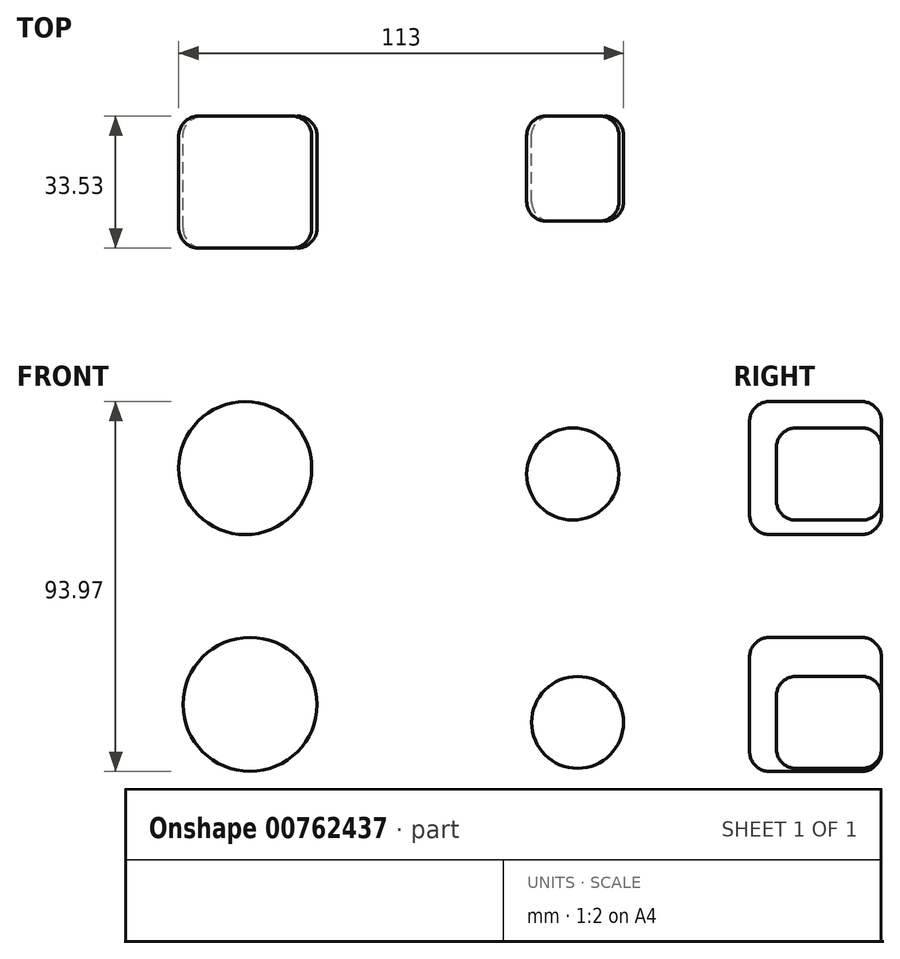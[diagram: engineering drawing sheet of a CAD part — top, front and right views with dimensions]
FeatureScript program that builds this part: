
annotation { "Feature Type Name" : "Feature", "Feature Type Description" : "" }
export const myFeature = defineFeature(function(context is Context, id is Id, definition is map)
    precondition{}
    {
        {
            var Q0;
            Q0=qCreatedBy(makeId("Front.planeOp"),FACE);
            var sketch = newSketch(context, id + "F0", { "sketchPlane" : qUnion([Q0])});
            skCircle(sketch, "E0", {"center": v(-51.36, 33.22) * mm, "radius": 16.9 * mm});
            skCircle(sketch, "E1", {"center": v(-50.14, -26.82) * mm, "radius": 17.03 * mm});
            skCircle(sketch, "E2", {"center": v(31.85, 31.7) * mm, "radius": 11.71 * mm});
            skCircle(sketch, "E3", {"center": v(33.07, -31.4) * mm, "radius": 11.67 * mm});
            skSolve(sketch);
        }
        {
            var Q0;
            Q0=makeQuery(id+"F0.imprint","IMPRINT",FACE,{"disambiguationData":[TD([[makeQuery(id+"F0.imprint","IMPRINT",EDGE,{"derivedFrom":sQuery(id+"F0.wireOp",EDGE,"E1")}),1.0]])]});
            var Q1;
            Q1=makeQuery(id+"F0.imprint","IMPRINT",FACE,{"disambiguationData":[TD([[makeQuery(id+"F0.imprint","IMPRINT",EDGE,{"derivedFrom":sQuery(id+"F0.wireOp",EDGE,"E0")}),1.0]])]});
            extrude(context, id + "F1", {"entities" : qUnion([Q0, Q1]), "depth" : 33.53 * mm, "offsetDistance" : 25.4 * mm});
        }
        {
            var Q0;
            Q0=makeQuery(id+"F1.opExtrude","CAP_EDGE",EDGE,{"disambiguationData":[OSD([sQuery(id+"F0.wireOp",EDGE,"E0")])],"isStart":false});
            var Q1;
            Q1=makeQuery(id+"F1.opExtrude","CAP_EDGE",EDGE,{"disambiguationData":[OSD([sQuery(id+"F0.wireOp",EDGE,"E0")])],"isStart":true});
            var Q2;
            Q2=makeQuery(id+"F1.opExtrude","CAP_EDGE",EDGE,{"disambiguationData":[OSD([sQuery(id+"F0.wireOp",EDGE,"E1")])],"isStart":false});
            var Q3;
            Q3=makeQuery(id+"F1.opExtrude","CAP_EDGE",EDGE,{"disambiguationData":[OSD([sQuery(id+"F0.wireOp",EDGE,"E1")])],"isStart":true});
            fillet(context, id + "F2", {"entities" : qUnion([Q0, Q1, Q2, Q3]), "radius" : 5.08 * mm, "tangentPropagation" : true, "allowEdgeOverflow" : false});
        }
        {
            var Q0;
            Q0=makeQuery(id+"F0.imprint","IMPRINT",FACE,{"disambiguationData":[TD([[makeQuery(id+"F0.imprint","IMPRINT",EDGE,{"derivedFrom":sQuery(id+"F0.wireOp",EDGE,"E3")}),1.0]])]});
            var Q1;
            Q1=makeQuery(id+"F0.imprint","IMPRINT",FACE,{"disambiguationData":[TD([[makeQuery(id+"F0.imprint","IMPRINT",EDGE,{"derivedFrom":sQuery(id+"F0.wireOp",EDGE,"E2")}),1.0]])]});
            extrude(context, id + "F3", {"entities" : qUnion([Q0, Q1]), "depth" : 26.67 * mm, "offsetDistance" : 25.4 * mm});
        }
        {
            var Q0;
            Q0=makeQuery(id+"F3.opExtrude","CAP_EDGE",EDGE,{"disambiguationData":[OSD([sQuery(id+"F0.wireOp",EDGE,"E3")])],"isStart":true});
            var Q1;
            Q1=makeQuery(id+"F3.opExtrude","CAP_EDGE",EDGE,{"disambiguationData":[OSD([sQuery(id+"F0.wireOp",EDGE,"E3")])],"isStart":false});
            var Q2;
            Q2=makeQuery(id+"F3.opExtrude","CAP_EDGE",EDGE,{"disambiguationData":[OSD([sQuery(id+"F0.wireOp",EDGE,"E2")])],"isStart":false});
            var Q3;
            Q3=makeQuery(id+"F3.opExtrude","CAP_EDGE",EDGE,{"disambiguationData":[OSD([sQuery(id+"F0.wireOp",EDGE,"E2")])],"isStart":true});
            fillet(context, id + "F4", {"entities" : qUnion([Q0, Q1, Q2, Q3]), "radius" : 4.9 * mm, "tangentPropagation" : true, "allowEdgeOverflow" : false});
        }
    });
